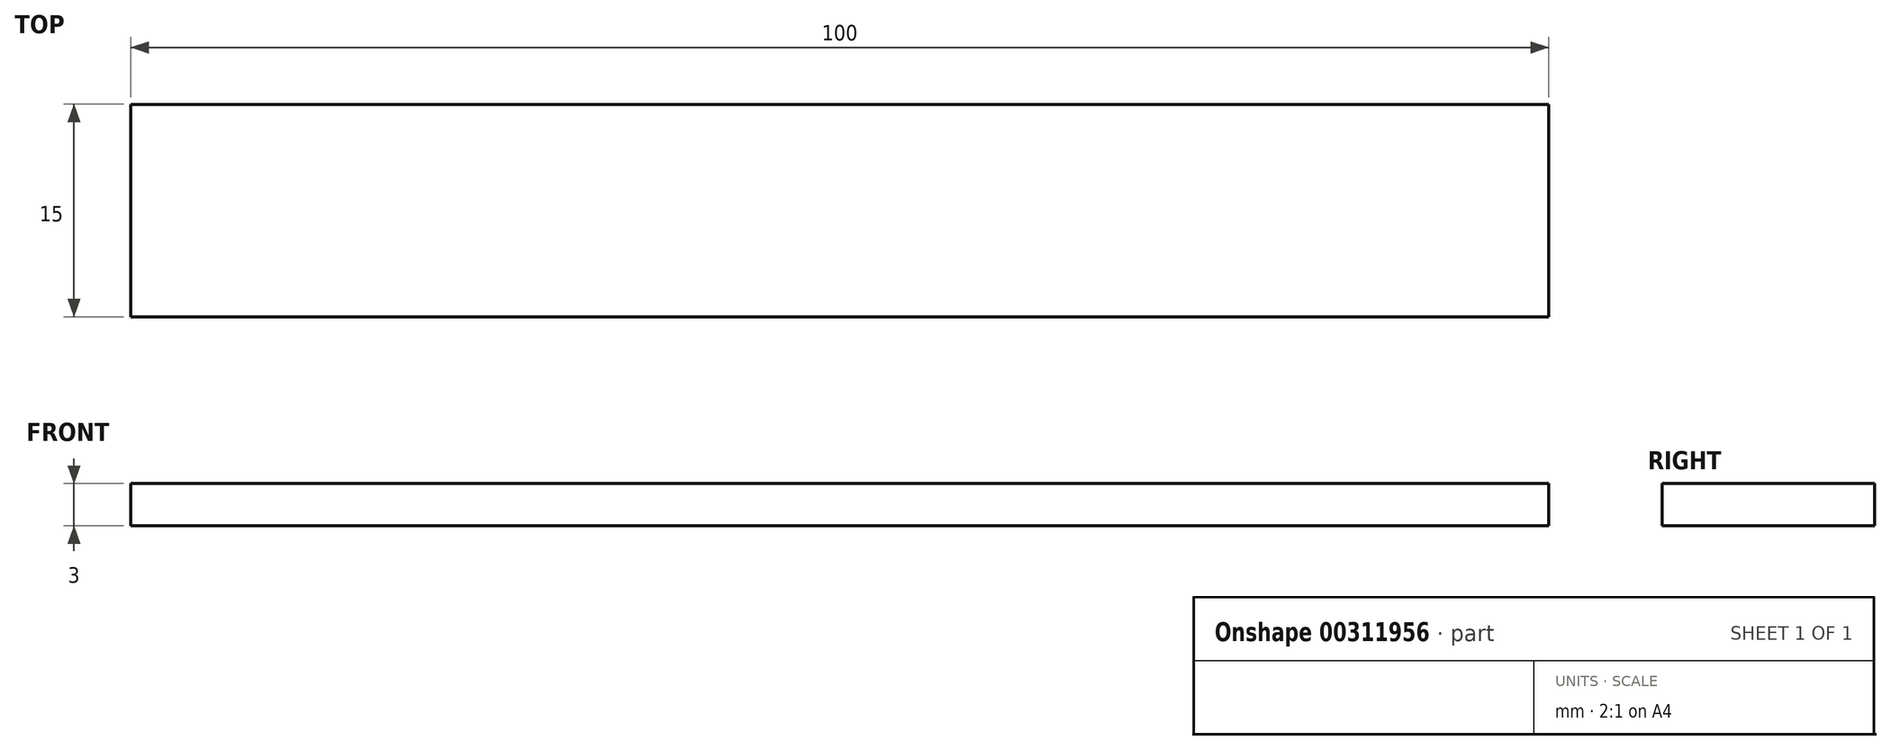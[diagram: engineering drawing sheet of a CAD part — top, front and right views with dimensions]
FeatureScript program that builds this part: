
annotation { "Feature Type Name" : "Feature", "Feature Type Description" : "" }
export const myFeature = defineFeature(function(context is Context, id is Id, definition is map)
    precondition{}
    {
        {
            var Q0;
            Q0=qCreatedBy(makeId("Top.planeOp"),FACE);
            var sketch = newSketch(context, id + "F0", { "sketchPlane" : qUnion([Q0])});
            skLineSegment(sketch, "E0.bottom", {"start": v(-47.4, 7.28) * mm, "end": v(52.6, 7.28) * mm});
            skLineSegment(sketch, "E0.top", {"start": v(-47.4, -7.72) * mm, "end": v(52.6, -7.72) * mm});
            skLineSegment(sketch, "E0.left", {"start": v(-47.4, 7.28) * mm, "end": v(-47.4, -7.72) * mm});
            skLineSegment(sketch, "E0.right", {"start": v(52.6, 7.28) * mm, "end": v(52.6, -7.72) * mm});
            skPoint(sketch, "E1", {"position": v(-37.77, 0) * mm});
            skPoint(sketch, "E2", {"position": v(-17.23, 0) * mm});
            skPoint(sketch, "E3", {"position": v(13.16, 0) * mm});
            skPoint(sketch, "E4", {"position": v(25.36, 0) * mm});
            skPoint(sketch, "E5", {"position": v(38.41, 0) * mm});
            skSolve(sketch);
        }
        {
            var Q0;
            Q0=makeQuery(id+"F0.imprint","IMPRINT",FACE,{"disambiguationData":[TD([[makeQuery(id+"F0.imprint","IMPRINT",EDGE,{"derivedFrom":sQuery(id+"F0.wireOp",EDGE,"E0.bottom")}),-1.0]])]});
            extrude(context, id + "F1", {"entities" : qUnion([Q0]), "depth" : 3 * mm});
        }
    });
